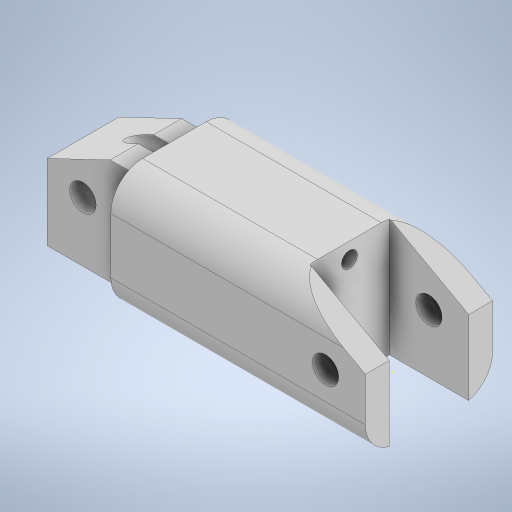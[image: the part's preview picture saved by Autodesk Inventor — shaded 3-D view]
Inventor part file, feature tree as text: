
AUTODESK INVENTOR PART (.ipt)
format: ipt  version: 2024 (Build 280153020, 153B)  size: 457,728 bytes
history: native  units: mm
features: sketch x21, extrude x18, chamfer x3, move_body x3, plane x2, split x2, boolean_combine x1, fillet x1
ambient origin geometry x8: Origin, YZ Plane, XZ Plane, XY Plane, X Axis, Y Axis, Z Axis, Center Point
bodies: Solid1 (feature_tree), Solid2 (feature_tree), Solid3 (feature_tree), Solid4 (feature_tree), Solid5 (feature_tree)
feature tree (51):
  extrude  "Extrusion1"  Depth=16.0mm
  sketch  "Sketch2"  dims[d2=15.0mm d3=0.0mm d4=10.0mm]
  extrude  "Extrusion2"  Depth=10.0mm
  chamfer  "Chamfer1"  Distance=21.25mm
  extrude  "Extrusion3"  Depth=10.0mm TaperAngle=0.0deg
  extrude  "Extrusion4"  Depth=11.5mm TaperAngle=0.0deg
  extrude  "Extrusion5"  Depth=1.0mm TaperAngle=0.0deg
  chamfer  "Chamfer2"  Distance=6.0mm Angle=45.0deg
  sketch  "Sketch6"  dims[d14=7.0mm d15=11.5mm d16=0.0mm]
  extrude  "Extrusion6"  Depth=9.0mm
  extrude  "Extrusion7"  Depth=11.5mm TaperAngle=0.0deg
  chamfer  "Chamfer3"  Distance=11.5mm Angle=45.0deg
  sketch  "Sketch9"  dims[d26=3.3mm d27=45.25mm d28=0.0mm d29=11.5mm d30=5.5mm d31=45.0deg]
  extrude  "Extrusion8"  Depth=65.75mm TaperAngle=0.0deg
  extrude  "Extrusion9"  Depth=9.0mm TaperAngle=0.0deg
  extrude  "Extrusion10"  Depth=13.0mm TaperAngle=0.0deg
  sketch  "Sketch13"  dims[d43=24.0mm d44=21.0mm d45=0.0mm]
  extrude  "Extrusion11"  Depth=21.0mm TaperAngle=0.0deg
  extrude  "Extrusion12"  TaperAngle=0.0deg  [1 undecoded]
  extrude  "Extrusion13"  Depth=6.0mm TaperAngle=0.0deg
  plane  "Work Plane1"
  split  "Split1"
  move_body  "Move Body1"
  extrude  "Extrusion14"  Depth=10.0mm TaperAngle=0.0deg
  move_body  "Move Body2"
  extrude  "Extrusion15"  TaperAngle=0.0deg  [1 undecoded]
  plane  "Work Plane2"
  split  "Split2"
  move_body  "Move Body3"
  boolean_combine  "Combine1"
  fillet  "Fillet2"  Radius=4.0mm
  extrude  "Extrusion16"  Depth=0.5mm TaperAngle=0.0deg
  extrude  "Extrusion17"  Depth=10.0mm TaperAngle=0.0deg
  extrude  "Extrusion18"  [1 undecoded]
  sketch  "Sketch1"  dims[d0=36.0mm d1=16.0mm]
  sketch  "Sketch3"  dims[d5=10.0mm]
  sketch  "Sketch4"  dims[d6=3.3mm d7=21.25mm d8=0.0mm]
  sketch  "Sketch5"  dims[d9=10.0mm d10=5.5mm d11=45.0deg d12=10.0mm d13=0.0mm]
  sketch  "Sketch7"  dims[d17=3.3mm d18=1.0mm d19=0.0mm d20=6.0mm d21=11.5mm d22=45.0deg]
  sketch  "Sketch8"  dims[d23=15.0mm d24=0.0mm d25=9.0mm]
  sketch  "Sketch10"  dims[d32=2.0mm d33=65.75mm d34=0.0mm]
  sketch  "Sketch11"  dims[d35=0.5mm d36=0.0mm d37=9.0mm d38=0.0mm]
  sketch  "Sketch12"  dims[d39=0.5mm d40=0.0mm d41=13.0mm d42=0.0mm]
  sketch  "Sketch14"  dims[d46=12.25mm d47=-12.0mm d48=0.0mm d49=0.0mm]
  sketch  "Sketch15"  dims[d50=30.0mm d51=0.0mm d52=6.0mm d53=0.0mm d54=0.0mm]
  sketch  "Sketch16"  dims[d56=10.0mm d57=20.0mm d58=0.0mm]
  sketch  "Sketch17"  dims[d59=3.75mm d60=-10.0mm d61=0.0mm d62=0.0mm d63=4.0mm]
  sketch  "Sketch18"  dims[d64=0.5mm d65=0.0mm d66=0.5mm d67=0.0mm]
  sketch  "Sketch19"  dims[d68=4.0mm d69=10.0mm d70=0.0mm]
  sketch  "Sketch20"
  sketch  "Sketch21"
note: 3 required parameter values undecoded (feature->parameter linkage not recoverable at this tier; creation-order binding heuristic only, values carry confidence <= 0.55)
